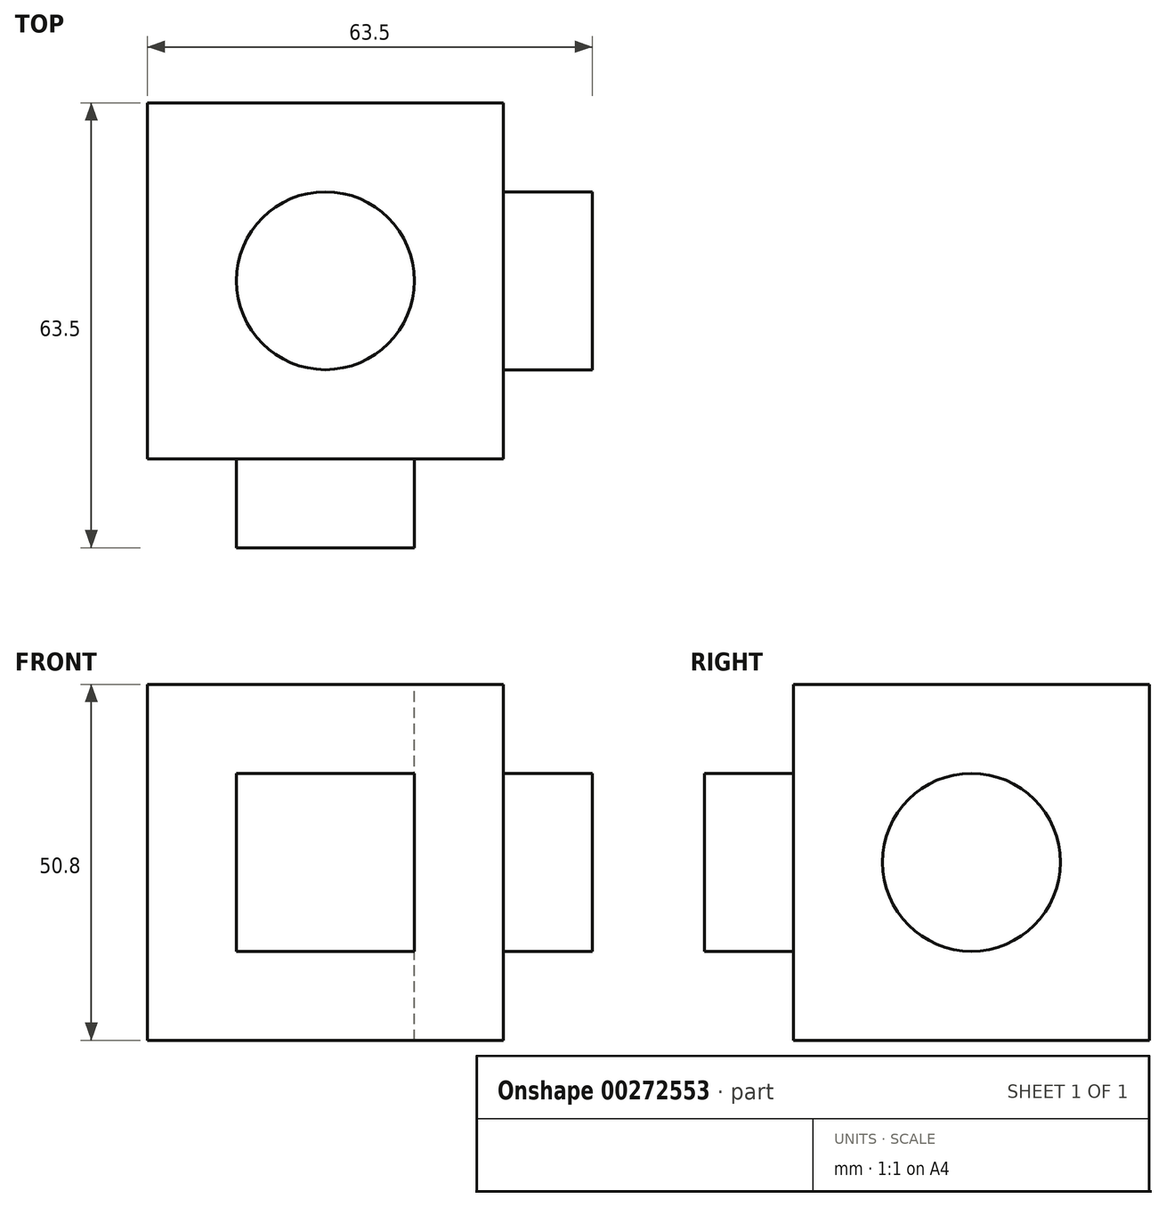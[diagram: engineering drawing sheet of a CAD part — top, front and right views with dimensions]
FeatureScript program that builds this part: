
annotation { "Feature Type Name" : "Feature", "Feature Type Description" : "" }
export const myFeature = defineFeature(function(context is Context, id is Id, definition is map)
    precondition{}
    {
        {
            var Q0;
            Q0=qCreatedBy(makeId("Front.planeOp"),FACE);
            var sketch = newSketch(context, id + "F0", { "sketchPlane" : qUnion([Q0])});
            skLineSegment(sketch, "E0.bottom", {"start": v(0, 0) * mm, "end": v(-50.8, 0) * mm});
            skLineSegment(sketch, "E0.top", {"start": v(0, 50.8) * mm, "end": v(-50.8, 50.8) * mm});
            skLineSegment(sketch, "E0.left", {"start": v(0, 0) * mm, "end": v(0, 50.8) * mm});
            skLineSegment(sketch, "E0.right", {"start": v(-50.8, 0) * mm, "end": v(-50.8, 50.8) * mm});
            skSolve(sketch);
        }
        {
            var Q0;
            Q0 = qSketchRegion(id + "F0", true);
            extrude(context, id + "F1", {"entities" : qUnion([Q0]), "depth" : 50.8 * mm});
        }
        {
            var Q0;
            Q0=makeQuery(id+"F1.opExtrude","SWEPT_FACE",FACE,{"disambiguationData":[OSD([sQuery(id+"F0.wireOp",EDGE,"E0.top")])]});
            var sketch = newSketch(context, id + "F2", { "sketchPlane" : qUnion([Q0])});
            skCircle(sketch, "E1", {"center": v(-25.4, -25.4) * mm, "radius": 12.7 * mm});
            skSolve(sketch);
        }
        {
            var Q0;
            Q0 = qSketchRegion(id + "F2", true);
            extrude(context, id + "F3", {"entities" : qUnion([Q0]), "operationType" : NewBodyOperationType.REMOVE, "oppositeDirection" : true, "depth" : 50.8 * mm});
        }
        {
            var Q0;
            Q0=makeQuery(id+"F1.opExtrude","SWEPT_FACE",FACE,{"disambiguationData":[OSD([sQuery(id+"F0.wireOp",EDGE,"E0.left")])]});
            var sketch = newSketch(context, id + "F4", { "sketchPlane" : qUnion([Q0])});
            skCircle(sketch, "E2", {"center": v(-25.4, 25.4) * mm, "radius": 12.7 * mm});
            skSolve(sketch);
        }
        {
            var Q0;
            Q0 = qSketchRegion(id + "F4", true);
            extrude(context, id + "F5", {"entities" : qUnion([Q0]), "operationType" : NewBodyOperationType.ADD, "depth" : 12.7 * mm});
        }
        {
            var Q0;
            Q0=makeQuery(id+"F1.opExtrude","CAP_FACE",FACE,{"disambiguationData":[OSD([sQuery(id+"F0.wireOp",EDGE,"E0.bottom"),sQuery(id+"F0.wireOp",EDGE,"E0.top"),sQuery(id+"F0.wireOp",EDGE,"E0.left"),sQuery(id+"F0.wireOp",EDGE,"E0.right")])],"isStart":false});
            var sketch = newSketch(context, id + "F6", { "sketchPlane" : qUnion([Q0])});
            skLineSegment(sketch, "E3.bottom", {"start": v(0, 0) * mm, "end": v(-25.4, 0) * mm});
            skLineSegment(sketch, "E3.left", {"start": v(0, 0) * mm, "end": v(0, 25.4) * mm});
            skLineSegment(sketch, "E4.bottom", {"start": v(-12.7, 12.7) * mm, "end": v(-38.1, 12.7) * mm});
            skLineSegment(sketch, "E4.top", {"start": v(-12.7, 38.1) * mm, "end": v(-38.1, 38.1) * mm});
            skLineSegment(sketch, "E4.left", {"start": v(-12.7, 12.7) * mm, "end": v(-12.7, 38.1) * mm});
            skLineSegment(sketch, "E4.right", {"start": v(-38.1, 12.7) * mm, "end": v(-38.1, 38.1) * mm});
            skSolve(sketch);
        }
        {
            var Q0;
            Q0 = qSketchRegion(id + "F6", true);
            extrude(context, id + "F7", {"entities" : qUnion([Q0]), "operationType" : NewBodyOperationType.ADD, "depth" : 12.7 * mm});
        }
    });
